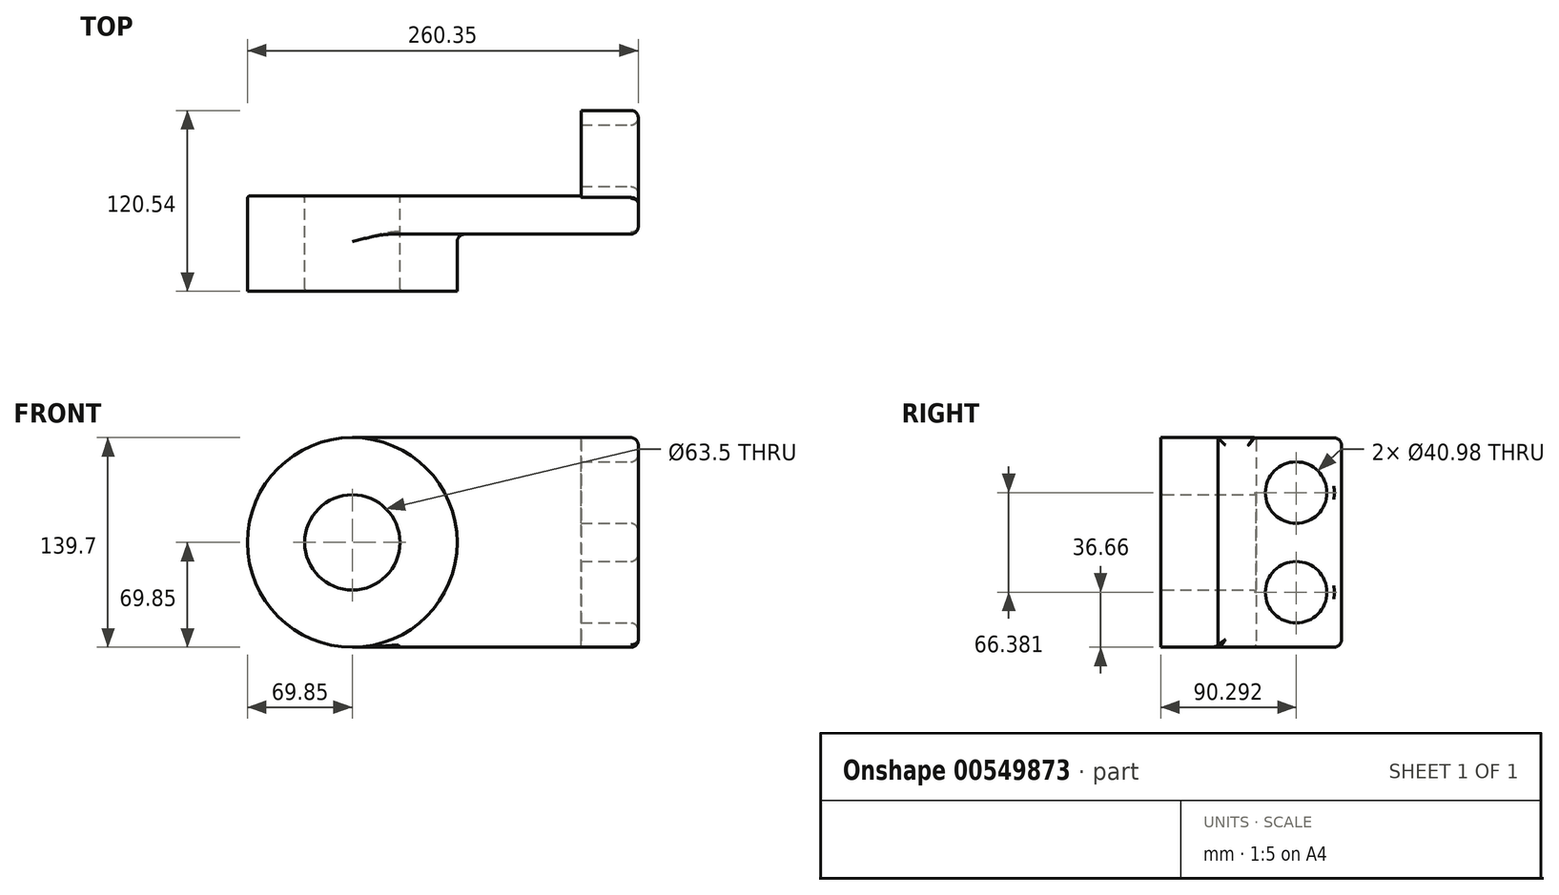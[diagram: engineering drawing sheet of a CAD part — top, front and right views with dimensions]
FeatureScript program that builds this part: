
annotation { "Feature Type Name" : "Feature", "Feature Type Description" : "" }
export const myFeature = defineFeature(function(context is Context, id is Id, definition is map)
    precondition{}
    {
        {
            var Q0;
            Q0=qCreatedBy(makeId("Front.planeOp"),FACE);
            var sketch = newSketch(context, id + "F0", { "sketchPlane" : qUnion([Q0])});
            skLineSegment(sketch, "E0.bottom", {"start": v(-95.25, 69.85) * mm, "end": v(95.25, 69.85) * mm});
            skLineSegment(sketch, "E0.top", {"start": v(-95.25, -69.85) * mm, "end": v(95.25, -69.85) * mm});
            skLineSegment(sketch, "E0.left", {"start": v(-95.25, 69.85) * mm, "end": v(-95.25, -69.85) * mm});
            skLineSegment(sketch, "E0.right", {"start": v(95.25, 69.85) * mm, "end": v(95.25, -69.85) * mm});
            skPoint(sketch, "E0.middle", {"position": v(0, 0) * mm});
            skCircle(sketch, "E1", {"center": v(-95.25, 0) * mm, "radius": 69.85 * mm});
            skCircle(sketch, "E2", {"center": v(-95.25, 0) * mm, "radius": 31.75 * mm});
            skSolve(sketch);
        }
        {
            var Q0;
            {var subQ1=sQuery(id+"F0.wireOp",EDGE,"E0.left");var subQ3=sQuery(id+"F0.wireOp",EDGE,"E2");var subQ4=makeQuery(id+"F0.imprint","INTERSECT",VERTEX,{"disambiguationData":[OD(0.0)],"derivedFrom":[subQ1,subQ3]});Q0=makeQuery(id+"F0.imprint","IMPRINT",FACE,{"disambiguationData":[TD([[makeQuery(id+"F0.imprint","IMPRINT",EDGE,{"disambiguationData":[TD([[subQ4,-1.0]])],"derivedFrom":subQ3}),-1.0]])]});}
            var Q1;
            {var subQ1=sQuery(id+"F0.wireOp",EDGE,"E0.left");var subQ3=sQuery(id+"F0.wireOp",EDGE,"E2");var subQ4=makeQuery(id+"F0.imprint","INTERSECT",VERTEX,{"disambiguationData":[OD(0.0)],"derivedFrom":[subQ1,subQ3]});Q1=makeQuery(id+"F0.imprint","IMPRINT",FACE,{"disambiguationData":[TD([[makeQuery(id+"F0.imprint","IMPRINT",EDGE,{"disambiguationData":[TD([[subQ4,1.0]])],"derivedFrom":subQ3}),-1.0]])]});}
            var Q2;
            {var subQ0=sQuery(id+"F0.wireOp",EDGE,"E0.bottom");Q2=makeQuery(id+"F0.imprint","IMPRINT",FACE,{"disambiguationData":[TD([[makeQuery(id+"F0.imprint","IMPRINT",EDGE,{"derivedFrom":subQ0}),-1.0]])]});}
            extrude(context, id + "F1", {"entities" : qUnion([Q0, Q1, Q2]), "depth" : 25.4 * mm, "offsetDistance" : 25.4 * mm});
        }
        {
            var Q0;
            Q0=makeQuery(id+"F1.opExtrude","SWEPT_FACE",FACE,{"disambiguationData":[OSD([sQuery(id+"F0.wireOp",EDGE,"E0.right")])]});
            var sketch = newSketch(context, id + "F2", { "sketchPlane" : qUnion([Q0])});
            skLineSegment(sketch, "E3.bottom", {"start": v(-25.4, -69.85) * mm, "end": v(57.04, -69.85) * mm});
            skLineSegment(sketch, "E3.top", {"start": v(-25.4, 69.74) * mm, "end": v(57.04, 69.74) * mm});
            skLineSegment(sketch, "E3.left", {"start": v(-25.4, -69.85) * mm, "end": v(-25.4, 69.74) * mm});
            skLineSegment(sketch, "E3.right", {"start": v(57.04, -69.85) * mm, "end": v(57.04, 69.74) * mm});
            skCircle(sketch, "E4", {"center": v(26.8, -33.2) * mm, "radius": 20.5 * mm});
            skLineSegment(sketch, "E5", {"start": v(0, 0) * mm, "end": v(57.04, 0) * mm, "construction": true});
            skCircle(sketch, "E6.MirrorC", {"center": v(26.8, 33.2) * mm, "radius": 20.5 * mm});
            skSolve(sketch);
        }
        {
            var Q0;
            {var subQ0=sQuery(id+"F2.wireOp",EDGE,"E3.right");Q0=makeQuery(id+"F2.imprint","IMPRINT",FACE,{"disambiguationData":[TD([[makeQuery(id+"F2.imprint","IMPRINT",EDGE,{"derivedFrom":subQ0}),1.0]])]});}
            extrude(context, id + "F3", {"entities" : qUnion([Q0]), "operationType" : NewBodyOperationType.ADD, "oppositeDirection" : true, "depth" : 38.1 * mm, "offsetDistance" : 25.4 * mm});
        }
        {
            var Q0;
            {var subQ1=sQuery(id+"F0.wireOp",EDGE,"E0.left");var subQ3=sQuery(id+"F0.wireOp",EDGE,"E2");var subQ4=makeQuery(id+"F0.imprint","INTERSECT",VERTEX,{"disambiguationData":[OD(0.0)],"derivedFrom":[subQ1,subQ3]});Q0=makeQuery(id+"F0.imprint","IMPRINT",FACE,{"disambiguationData":[TD([[makeQuery(id+"F0.imprint","IMPRINT",EDGE,{"disambiguationData":[TD([[subQ4,1.0]])],"derivedFrom":subQ3}),-1.0]])]});}
            var Q1;
            {var subQ1=sQuery(id+"F0.wireOp",EDGE,"E0.left");var subQ3=sQuery(id+"F0.wireOp",EDGE,"E2");var subQ4=makeQuery(id+"F0.imprint","INTERSECT",VERTEX,{"disambiguationData":[OD(0.0)],"derivedFrom":[subQ1,subQ3]});Q1=makeQuery(id+"F0.imprint","IMPRINT",FACE,{"disambiguationData":[TD([[makeQuery(id+"F0.imprint","IMPRINT",EDGE,{"disambiguationData":[TD([[subQ4,-1.0]])],"derivedFrom":subQ3}),-1.0]])]});}
            extrude(context, id + "F4", {"entities" : qUnion([Q0, Q1]), "operationType" : NewBodyOperationType.ADD, "depth" : 63.5 * mm, "offsetDistance" : 25.4 * mm});
        }
        {
            var Q0;
            {var subQ0=sQuery(id+"F0.wireOp",EDGE,"E1");Q0=makeQuery(id+"F4.boolean.opBoolean","INTERSECT",EDGE,{"derivedFrom":[makeQuery(id+"F1.opExtrude","CAP_FACE",FACE,{"disambiguationData":[OSD([sQuery(id+"F0.wireOp",EDGE,"E0.bottom"),sQuery(id+"F0.wireOp",EDGE,"E0.top"),sQuery(id+"F0.wireOp",EDGE,"E0.right"),subQ0,sQuery(id+"F0.wireOp",EDGE,"E2")])],"isStart":false}),makeQuery(id+"F4.opExtrude","SWEPT_FACE",FACE,{"disambiguationData":[OSD([subQ0])]})]});}
            var Q1;
            Q1=makeQuery(id+"F1.opExtrude","CAP_EDGE",EDGE,{"disambiguationData":[OSD([sQuery(id+"F0.wireOp",EDGE,"E0.right")])],"isStart":false});
            var Q2;
            Q2=makeQuery(id+"F3.opExtrude","SWEPT_EDGE",EDGE,{"disambiguationData":[OSD([sQuery(id+"F2.wireOp",EDGE,"E3.bottom"),sQuery(id+"F2.wireOp",EDGE,"E3.right")])]});
            var Q3;
            Q3=makeQuery(id+"F3.opExtrude","SWEPT_EDGE",EDGE,{"disambiguationData":[OSD([sQuery(id+"F2.wireOp",EDGE,"E3.top"),sQuery(id+"F2.wireOp",EDGE,"E3.right")])]});
            var Q4;
            {var subQ0=sQuery(id+"F0.wireOp",EDGE,"E0.right");Q4=makeQuery(id+"F3.boolean.opBoolean","MERGE",FACE,{"derivedFrom":[makeQuery(id+"F1.opExtrude","SWEPT_FACE",FACE,{"disambiguationData":[OSD([subQ0])]}),makeQuery(id+"F3.opExtrude","CAP_FACE",FACE,{"disambiguationData":[OSD([subQ0,sQuery(id+"F2.wireOp",EDGE,"E3.bottom"),sQuery(id+"F2.wireOp",EDGE,"E3.top"),sQuery(id+"F2.wireOp",EDGE,"E3.right"),sQuery(id+"F2.wireOp",EDGE,"E4"),sQuery(id+"F2.wireOp",EDGE,"E6.MirrorC")])],"isStart":true})]});}
            fillet(context, id + "F5", {"entities" : qUnion([Q0, Q1, Q2, Q3, Q4]), "radius" : 5.08 * mm, "tangentPropagation" : true, "allowEdgeOverflow" : false});
        }
        {
            var Q0;
            Q0=makeQuery(id+"F1.opExtrude","CAP_EDGE",EDGE,{"disambiguationData":[OSD([sQuery(id+"F0.wireOp",EDGE,"E0.top")])],"isStart":false});
            var Q1;
            Q1=makeQuery(id+"F1.opExtrude","CAP_EDGE",EDGE,{"disambiguationData":[OSD([sQuery(id+"F0.wireOp",EDGE,"E0.top")])],"isStart":true});
            var Q2;
            Q2=makeQuery(id+"F3.opExtrude","CAP_EDGE",EDGE,{"disambiguationData":[OSD([sQuery(id+"F0.wireOp",EDGE,"E0.right")])],"isStart":false});
            fillet(context, id + "F6", {"entities" : qUnion([Q0, Q1, Q2]), "radius" : 1.59 * mm, "tangentPropagation" : true, "allowEdgeOverflow" : false});
        }
        {
            var Q0;
            {var subQ0=sQuery(id+"F0.wireOp",EDGE,"E2");Q0=makeQuery(id+"F4.boolean.opBoolean","MERGE",FACE,{"derivedFrom":[makeQuery(id+"F1.opExtrude","SWEPT_FACE",FACE,{"disambiguationData":[OSD([subQ0])]}),makeQuery(id+"F4.opExtrude","SWEPT_FACE",FACE,{"disambiguationData":[OSD([subQ0])]})]});}
            fillet(context, id + "F7", {"entities" : qUnion([Q0]), "radius" : 1.59 * mm, "tangentPropagation" : true, "allowEdgeOverflow" : false});
        }
    });
